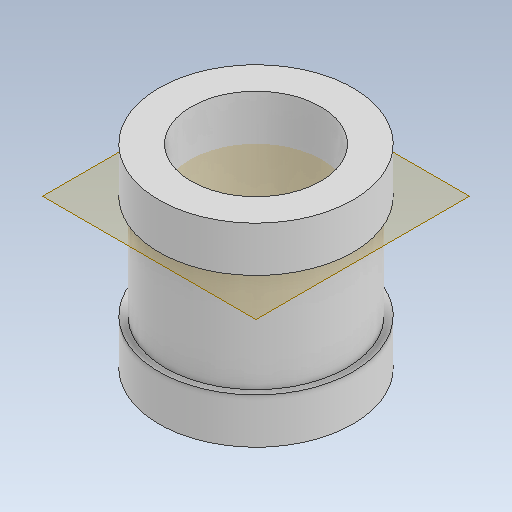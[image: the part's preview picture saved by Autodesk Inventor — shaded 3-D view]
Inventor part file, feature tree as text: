
AUTODESK INVENTOR PART (.ipt)
format: ipt  version: 2020 (Build 240168000, 168)  size: 126,464 bytes
history: native  units: mm
features: extrude x2, sketch x2, plane x1, projected_geometry x1
ambient origin geometry x8: Origin, YZ Plane, XZ Plane, XY Plane, X Axis, Y Axis, Z Axis, Center Point
bodies: Solid1 (feature_tree)
feature tree (6):
  extrude  "Extrusion1"  Depth=3.0mm
  plane  "Work Plane1"
  extrude  "Extrusion2"  [1 undecoded]
  sketch  "Sketch1"  dims[d0=3.0mm d1=2.0mm]
  sketch  "Sketch2"  dims[d2=3.0mm d3=0.0mm d4=-0.7mm d5=2.8mm d6=1.6mm d7=0.0mm]
  projected_geometry  "Projected Loop1"
note: 1 required parameter value undecoded (feature->parameter linkage not recoverable at this tier; creation-order binding heuristic only, values carry confidence <= 0.55)
